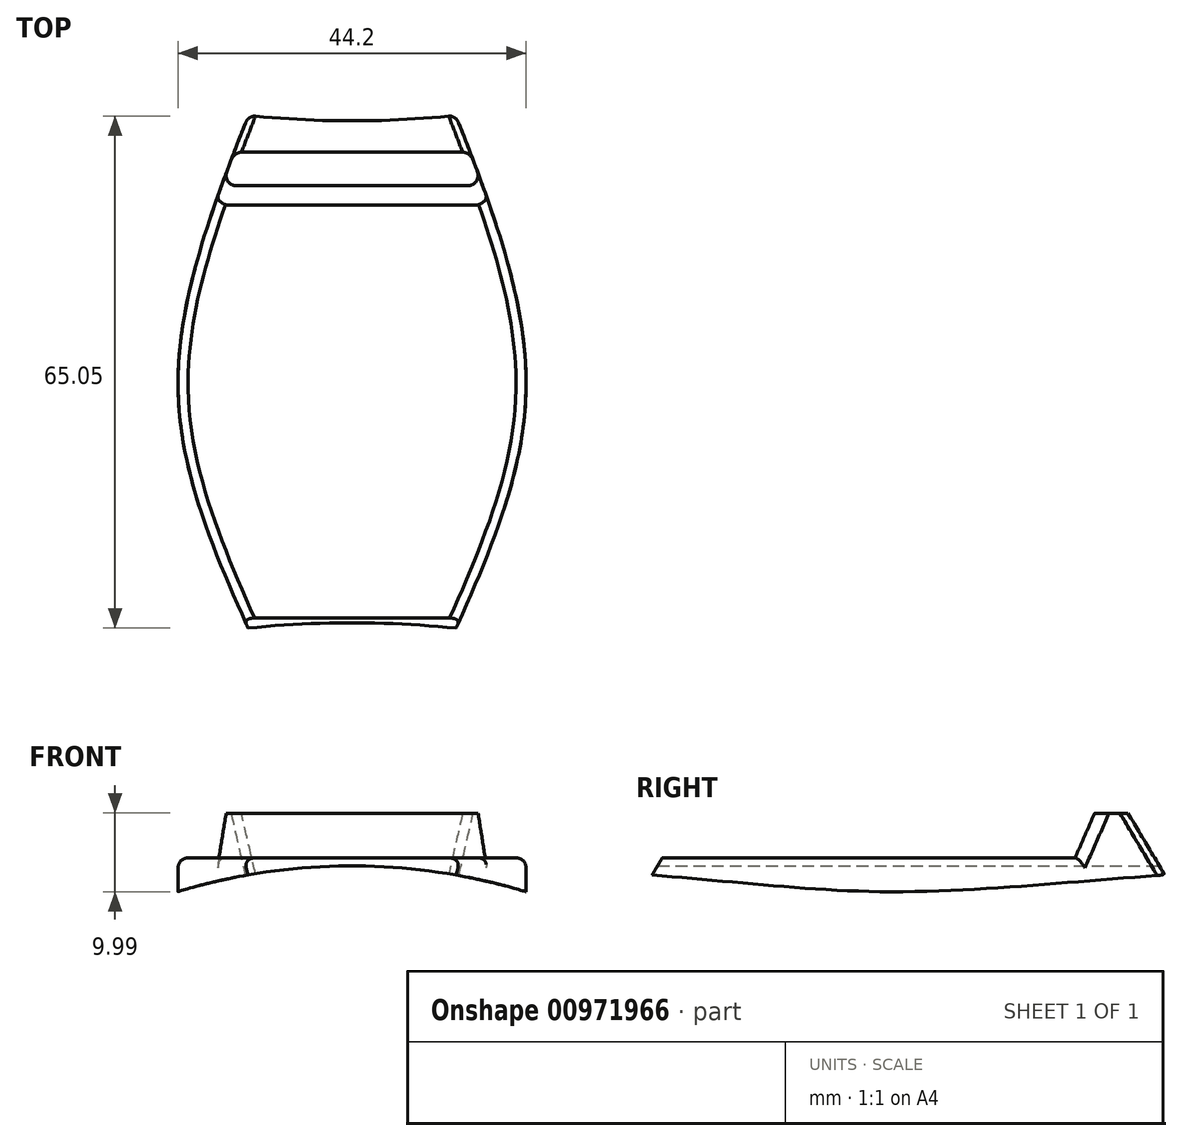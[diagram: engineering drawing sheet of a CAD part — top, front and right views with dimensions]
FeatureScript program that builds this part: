
annotation { "Feature Type Name" : "Feature", "Feature Type Description" : "" }
export const myFeature = defineFeature(function(context is Context, id is Id, definition is map)
    precondition{}
    {
        {
            var Q0;
            Q0=qCreatedBy(makeId("Right.planeOp"),FACE);
            var sketch = newSketch(context, id + "F0", { "sketchPlane" : qUnion([Q0])});
            skLineSegment(sketch, "E0", {"start": v(-30.67, 0) * mm, "end": v(37.07, 0) * mm});
            skLineSegment(sketch, "E1", {"start": v(-17.97, 4.35) * mm, "end": v(24.37, 4.35) * mm});
            skLineSegment(sketch, "E2", {"start": v(37.07, 0) * mm, "end": v(31.1, 10.04) * mm});
            skLineSegment(sketch, "E3", {"start": v(31.1, 10.04) * mm, "end": v(26.86, 10.04) * mm});
            skLineSegment(sketch, "E4", {"start": v(26.86, 10.04) * mm, "end": v(24.37, 4.35) * mm});
            skLineSegment(sketch, "E5", {"start": v(3.2, 0) * mm, "end": v(3.2, 4.35) * mm});
            skLineSegment(sketch, "E6.bottom", {"start": v(-67.15, 50) * mm, "end": v(95.4, 50) * mm});
            skLineSegment(sketch, "E6.top", {"start": v(-67.15, -41.02) * mm, "end": v(95.4, -41.02) * mm});
            skLineSegment(sketch, "E6.left", {"start": v(-67.15, 50) * mm, "end": v(-67.15, -41.02) * mm});
            skLineSegment(sketch, "E6.right", {"start": v(95.4, 50) * mm, "end": v(95.4, -41.02) * mm});
            skLineSegment(sketch, "E7", {"start": v(-17.97, 4.35) * mm, "end": v(-28.07, 4.35) * mm});
            skLineSegment(sketch, "E8", {"start": v(-28.07, 4.35) * mm, "end": v(-30.67, 0) * mm});
            skSolve(sketch);
        }
        {
            var Q0;
            Q0=qCreatedBy(makeId("Top.planeOp"),FACE);
            var sketch = newSketch(context, id + "F1", { "sketchPlane" : qUnion([Q0])});
            skLineSegment(sketch, "E9", {"start": v(0, 11.41) * mm, "end": v(0, -9.41) * mm});
            skLineSegment(sketch, "E10", {"start": v(0, 1) * mm, "end": v(-22.1, 1) * mm});
            skLineSegment(sketch, "E11", {"start": v(0, 1) * mm, "end": v(0, -30.51) * mm});
            skLineSegment(sketch, "E12", {"start": v(0, -30.51) * mm, "end": v(0, 36.96) * mm});
            skLineSegment(sketch, "E13", {"start": v(0, 36.96) * mm, "end": v(-12.7, 36.96) * mm});
            skLineSegment(sketch, "E14", {"start": v(0, 36.96) * mm, "end": v(12.7, 36.96) * mm});
            skLineSegment(sketch, "E15", {"start": v(0, -30.51) * mm, "end": v(-12.7, -30.51) * mm});
            skLineSegment(sketch, "E16", {"start": v(0, -30.51) * mm, "end": v(12.7, -30.51) * mm});
            skLineSegment(sketch, "E17", {"start": v(0, 1) * mm, "end": v(22.1, 1) * mm});
            skFitSpline(sketch, "E18", {"points": [v(-12.7, 36.96) * mm, v(-22.1, 1) * mm, v(-12.7, -30.51) * mm], "startDerivative": vector(-27.93, -71.02) * mm, "endDerivative": vector(28.5, -63.86) * mm});
            skFitSpline(sketch, "E19", {"points": [v(12.7, 36.96) * mm, v(22.1, 1) * mm, v(12.7, -30.51) * mm], "startDerivative": vector(27.93, -71.02) * mm, "endDerivative": vector(-28.5, -63.86) * mm});
            skSolve(sketch);
        }
        {
            var Q0;
            {var subQ1=sQuery(id+"F1.wireOp",EDGE,"E16");Q0=makeQuery(id+"F1.imprint","IMPRINT",FACE,{"disambiguationData":[TD([[makeQuery(id+"F1.imprint","IMPRINT",EDGE,{"derivedFrom":subQ1}),1.0]])]});}
            var Q1;
            {var subQ0=sQuery(id+"F1.wireOp",EDGE,"E14");Q1=makeQuery(id+"F1.imprint","IMPRINT",FACE,{"disambiguationData":[TD([[makeQuery(id+"F1.imprint","IMPRINT",EDGE,{"derivedFrom":subQ0}),-1.0]])]});}
            var Q2;
            {var subQ3=sQuery(id+"F1.wireOp",EDGE,"E10");Q2=makeQuery(id+"F1.imprint","IMPRINT",FACE,{"disambiguationData":[TD([[makeQuery(id+"F1.imprint","IMPRINT",EDGE,{"derivedFrom":subQ3}),-1.0]])]});}
            var Q3;
            {var subQ2=sQuery(id+"F1.wireOp",EDGE,"E10");Q3=makeQuery(id+"F1.imprint","IMPRINT",FACE,{"disambiguationData":[TD([[makeQuery(id+"F1.imprint","IMPRINT",EDGE,{"derivedFrom":subQ2}),1.0]])]});}
            extrude(context, id + "F2", {"entities" : qUnion([Q0, Q1, Q2, Q3]), "depth" : 10.04 * mm, "offsetDistance" : 25.4 * mm});
        }
        {
            var Q0;
            {var subQ9=sQuery(id+"F0.wireOp",EDGE,"f0UAfcan-YOLZ-XBiN-rJME-h1AG6BsoBLqj");Q0=makeQuery(id+"F0.imprint","IMPRINT",FACE,{"disambiguationData":[TD([[makeQuery(id+"F0.imprint","IMPRINT",EDGE,{"derivedFrom":subQ9}),-1.0]])]});}
            var Q1;
            {var subQ1=sQuery(id+"F0.wireOp",EDGE,"E2");Q1=makeQuery(id+"F0.imprint","IMPRINT",FACE,{"disambiguationData":[TD([[makeQuery(id+"F0.imprint","IMPRINT",EDGE,{"derivedFrom":subQ1}),-1.0]])]});}
            extrude(context, id + "F3", {"entities" : qUnion([Q0, Q1]), "operationType" : NewBodyOperationType.REMOVE, "endBound" : BoundingType.SYMMETRIC, "oppositeDirection" : true, "depth" : 73.15 * mm, "offsetDistance" : 25.4 * mm});
        }
        {
            var Q0;
            Q0=makeQuery(id+"F3.boolean.opBoolean","INTERSECT",EDGE,{"derivedFrom":[makeQuery(id+"F2.opExtrude","SWEPT_FACE",FACE,{"disambiguationData":[OSD([sQuery(id+"F1.wireOp",EDGE,"E18")])]}),makeQuery(id+"F3.opExtrude","SWEPT_FACE",FACE,{"disambiguationData":[OSD([sQuery(id+"F0.wireOp",EDGE,"E1")])]})]});
            var Q1;
            Q1=makeQuery(id+"F3.boolean.opBoolean","INTERSECT",EDGE,{"derivedFrom":[makeQuery(id+"F2.opExtrude","SWEPT_FACE",FACE,{"disambiguationData":[OSD([sQuery(id+"F1.wireOp",EDGE,"E18")])]}),makeQuery(id+"F3.opExtrude","SWEPT_FACE",FACE,{"disambiguationData":[OSD([sQuery(id+"F0.wireOp",EDGE,"E4")])]})]});
            var Q2;
            Q2=makeQuery(id+"F3.boolean.opBoolean","INTERSECT",EDGE,{"derivedFrom":[makeQuery(id+"F2.opExtrude","SWEPT_FACE",FACE,{"disambiguationData":[OSD([sQuery(id+"F1.wireOp",EDGE,"E19")])]}),makeQuery(id+"F3.opExtrude","SWEPT_FACE",FACE,{"disambiguationData":[OSD([sQuery(id+"F0.wireOp",EDGE,"E4")])]})]});
            var Q3;
            Q3=makeQuery(id+"F3.boolean.opBoolean","INTERSECT",EDGE,{"derivedFrom":[makeQuery(id+"F2.opExtrude","SWEPT_FACE",FACE,{"disambiguationData":[OSD([sQuery(id+"F1.wireOp",EDGE,"E19")])]}),makeQuery(id+"F3.opExtrude","SWEPT_FACE",FACE,{"disambiguationData":[OSD([sQuery(id+"F0.wireOp",EDGE,"E1")])]})]});
            var Q4;
            Q4=makeQuery(id+"F3.boolean.opBoolean","INTERSECT",EDGE,{"derivedFrom":[makeQuery(id+"F2.opExtrude","SWEPT_FACE",FACE,{"disambiguationData":[OSD([sQuery(id+"F1.wireOp",EDGE,"E19")])]}),makeQuery(id+"F3.opExtrude","SWEPT_FACE",FACE,{"disambiguationData":[OSD([sQuery(id+"F0.wireOp",EDGE,"5HqzP0p4-EUWS-5hlx-exL3-PoZeFwzppDlw")])]})]});
            var Q5;
            Q5=makeQuery(id+"F3.boolean.opBoolean","COPY",EDGE,{"derivedFrom":makeQuery(id+"F3.opExtrude","SWEPT_EDGE",EDGE,{"disambiguationData":[OSD([sQuery(id+"F0.wireOp",EDGE,"7wv0nnnK-TNmH-RVlH-PWxV-5QK5uFxknzdq"),sQuery(id+"F0.wireOp",EDGE,"5HqzP0p4-EUWS-5hlx-exL3-PoZeFwzppDlw")])]})});
            var Q6;
            Q6=makeQuery(id+"F3.boolean.opBoolean","INTERSECT",EDGE,{"derivedFrom":[makeQuery(id+"F2.opExtrude","SWEPT_FACE",FACE,{"disambiguationData":[OSD([sQuery(id+"F1.wireOp",EDGE,"E18")])]}),makeQuery(id+"F3.opExtrude","SWEPT_FACE",FACE,{"disambiguationData":[OSD([sQuery(id+"F0.wireOp",EDGE,"5HqzP0p4-EUWS-5hlx-exL3-PoZeFwzppDlw")])]})]});
            var Q7;
            Q7=makeQuery(id+"F3.boolean.opBoolean","INTERSECT",EDGE,{"derivedFrom":[makeQuery(id+"F2.opExtrude","SWEPT_FACE",FACE,{"disambiguationData":[OSD([sQuery(id+"F1.wireOp",EDGE,"E18")])]}),makeQuery(id+"F3.opExtrude","SWEPT_FACE",FACE,{"disambiguationData":[OSD([sQuery(id+"F0.wireOp",EDGE,"f0UAfcan-YOLZ-XBiN-rJME-h1AG6BsoBLqj")])]})]});
            var Q8;
            Q8=makeQuery(id+"F3.boolean.opBoolean","INTERSECT",EDGE,{"derivedFrom":[makeQuery(id+"F2.opExtrude","SWEPT_FACE",FACE,{"disambiguationData":[OSD([sQuery(id+"F1.wireOp",EDGE,"E19")])]}),makeQuery(id+"F3.opExtrude","SWEPT_FACE",FACE,{"disambiguationData":[OSD([sQuery(id+"F0.wireOp",EDGE,"f0UAfcan-YOLZ-XBiN-rJME-h1AG6BsoBLqj")])]})]});
            var Q9;
            Q9=makeQuery(id+"F3.boolean.opBoolean","COPY",EDGE,{"derivedFrom":makeQuery(id+"F3.opExtrude","SWEPT_EDGE",EDGE,{"disambiguationData":[OSD([sQuery(id+"F0.wireOp",EDGE,"f0UAfcan-YOLZ-XBiN-rJME-h1AG6BsoBLqj"),sQuery(id+"F0.wireOp",EDGE,"7wv0nnnK-TNmH-RVlH-PWxV-5QK5uFxknzdq")])]})});
            var Q10;
            Q10=makeQuery(id+"F3.boolean.opBoolean","INTERSECT",EDGE,{"derivedFrom":[makeQuery(id+"F2.opExtrude","SWEPT_FACE",FACE,{"disambiguationData":[OSD([sQuery(id+"F1.wireOp",EDGE,"E18")])]}),makeQuery(id+"F3.opExtrude","SWEPT_FACE",FACE,{"disambiguationData":[OSD([sQuery(id+"F0.wireOp",EDGE,"E2")])]})]});
            var Q11;
            Q11=makeQuery(id+"F3.boolean.opBoolean","INTERSECT",EDGE,{"derivedFrom":[makeQuery(id+"F2.opExtrude","SWEPT_FACE",FACE,{"disambiguationData":[OSD([sQuery(id+"F1.wireOp",EDGE,"E19")])]}),makeQuery(id+"F3.opExtrude","SWEPT_FACE",FACE,{"disambiguationData":[OSD([sQuery(id+"F0.wireOp",EDGE,"E2")])]})]});
            var Q12;
            Q12=makeQuery(id+"F3.boolean.opBoolean","COPY",EDGE,{"derivedFrom":makeQuery(id+"F3.opExtrude","SWEPT_EDGE",EDGE,{"disambiguationData":[OSD([sQuery(id+"F0.wireOp",EDGE,"E2"),sQuery(id+"F0.wireOp",EDGE,"E3")])]})});
            fillet(context, id + "F4", {"entities" : qUnion([Q0, Q1, Q2, Q3, Q4, Q5, Q6, Q7, Q8, Q9, Q10, Q11, Q12]), "radius" : 1.27 * mm, "tangentPropagation" : true, "allowEdgeOverflow" : false});
        }
        {
            var Q0;
            Q0=qCreatedBy(makeId("Front.planeOp"),FACE);
            var sketch = newSketch(context, id + "F5", { "sketchPlane" : qUnion([Q0])});
            skLineSegment(sketch, "E20", {"start": v(22.83, -0.17) * mm, "end": v(22.83, -11.6) * mm});
            skLineSegment(sketch, "E21", {"start": v(-22.9, -11.6) * mm, "end": v(-22.9, -0.17) * mm});
            skLineSegment(sketch, "E22", {"start": v(22.83, -5.89) * mm, "end": v(-22.9, -5.89) * mm});
            skArc(sketch, "E23", {"start": v(22.83, -11.6) * mm, "mid": v(-0.04, -8.1) * mm, "end": v(-22.9, -11.6) * mm});
            skArc(sketch, "E24", {"start": v(22.83, -0.17) * mm, "mid": v(-0.04, 3.34) * mm, "end": v(-22.9, -0.17) * mm});
            skSolve(sketch);
        }
        {
            var Q0;
            {var subQ2=sQuery(id+"F5.wireOp",EDGE,"E22");Q0=makeQuery(id+"F5.imprint","IMPRINT",FACE,{"disambiguationData":[TD([[makeQuery(id+"F5.imprint","IMPRINT",EDGE,{"derivedFrom":subQ2}),-1.0]])]});}
            var Q1;
            {var subQ2=sQuery(id+"F5.wireOp",EDGE,"E22");Q1=makeQuery(id+"F5.imprint","IMPRINT",FACE,{"disambiguationData":[TD([[makeQuery(id+"F5.imprint","IMPRINT",EDGE,{"derivedFrom":subQ2}),1.0]])]});}
            extrude(context, id + "F6", {"entities" : qUnion([Q0, Q1]), "operationType" : NewBodyOperationType.REMOVE, "endBound" : BoundingType.SYMMETRIC, "depth" : 114.3 * mm, "offsetDistance" : 25.4 * mm});
        }
    });
